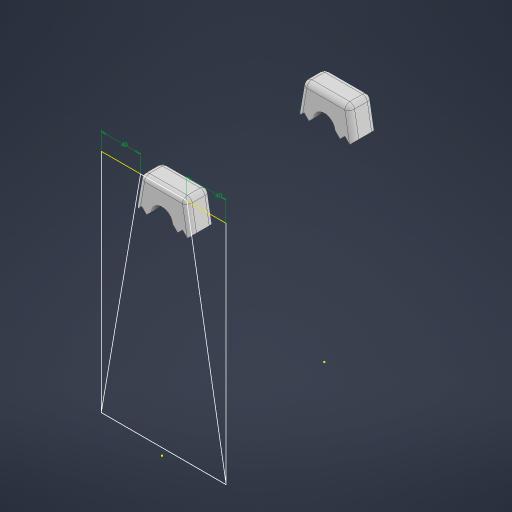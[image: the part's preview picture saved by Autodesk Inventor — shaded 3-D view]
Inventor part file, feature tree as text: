
AUTODESK INVENTOR PART (.ipt)
format: ipt  version: 2023 (Build 270158030, 158C)  size: 420,352 bytes
history: native  units: in
note: dims shown in document units (in); Inventor stores cm internally (conversion verified against a paired STEP export)
features: sketch x16, extrude x14, fillet x2, split x1
ambient origin geometry x8: Origin, YZ Plane, XZ Plane, XY Plane, X Axis, Y Axis, Z Axis, Center Point
bodies: Solid1 (feature_tree)
feature tree (33):
  extrude  "Extrusion1"  Depth=0.2756in TaperAngle=0.0deg
  extrude  "Extrusion2"  Depth=0.2756in TaperAngle=0.0deg
  sketch  "Sketch4"  dims[d10=5.0in d11=0.9055in]
  sketch  "Sketch5"  dims[d12=0.1969in d13=5.0in d14=0.9055in]
  sketch  "Sketch6"  dims[d16=2.7953in d17=9.0551in d18=0.0in]
  extrude  "Extrusion4"  Depth=0.9055in
  extrude  "Extrusion5"  Depth=0.9055in
  extrude  "Extrusion6"  Depth=9.0551in TaperAngle=0.0deg
  extrude  "Extrusion7"  Depth=1.9685in
  sketch  "Sketch9"  dims[d28=1.5748in d29=1.5748in]
  sketch  "Sketch10"  dims[d30=1.5748in d31=1.5748in]
  extrude  "Extrusion8"  Depth=0.8858in
  fillet  "Fillet1"  Radius=9.0551in
  fillet  "Fillet2"  Radius=7.2835in
  extrude  "Extrusion9"  Depth=1.5748in
  extrude  "Extrusion10"  Depth=1.5748in
  sketch  "Sketch16"  dims[d37=10.9085in d38=0.0in d39=0.2756in d40=0.0in]
  extrude  "Extrusion13"  Depth=0.1969in
  extrude  "Extrusion14"  Depth=0.1969in
  extrude  "Extrusion16"  Depth=0.2756in TaperAngle=0.0deg
  extrude  "Extrusion17"  Depth=0.3937in
  extrude  "Extrusion18"  Depth=0.3937in TaperAngle=0.0deg
  split  "Split1"
  sketch  "Sketch1"  dims[d0=9.4488in d1=0.2756in d2=0.0in]
  sketch  "Sketch2"  dims[d3=0.8583in d4=0.2756in d5=0.0in]
  sketch  "Sketch7"  dims[d19=9.0551in d20=0.0in d21=1.9685in]
  sketch  "Sketch8"  dims[d22=1.7717in d23=0.8858in d24=9.0551in d25=0.0in d26=7.2835in d27=0.0in]
  sketch  "Sketch11"  dims[d32=10.9085in d33=0.0in d34=0.1969in]
  sketch  "Sketch12"  dims[d35=0.1969in d36=0.8583in]
  sketch  "Sketch20"  dims[d51=1.7717in d52=0.3937in]
  sketch  "Sketch21"  dims[d53=2.7559in d54=0.3937in d55=0.0in]
  sketch  "Sketch22"  dims[d57=2.9528in]
  sketch  "Sketch23"  dims[d58=1.9685in d59=0.9449in d60=0.5118in d61=1.5026in d62=0.6299in d63=0.0in d66=2.7559in d67=3.3465in d68=0.0787in d69=0.0787in d70=0.0787in d71=0.4469in d72=0.0in d73=0.3346in d74=0.3346in d75=0.0787in d76=0.4469in d77=0.0in d80=1.9685in d81=1.8898in d82=0.4469in d83=0.0in d84=0.2756in d85=45.0deg d86=0.2756in d87=135.0deg d88=0.2756in d89=135.0deg d90=0.2756in d91=135.0deg d92=0.0984in d93=135.0deg d94=0.0in]
